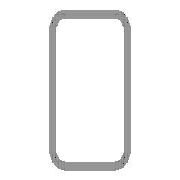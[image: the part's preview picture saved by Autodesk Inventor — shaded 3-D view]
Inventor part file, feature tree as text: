
AUTODESK INVENTOR PART (.ipt)
format: ipt  version: 2025.3 (Build 293356000, 356)  size: 149,504 bytes
history: native  units: mm (DEFAULTED — no unit token found)
features: other x4, plane x3, split x2, sketch x1
ambient origin geometry x8: Origin, YZ Plane, XZ Plane, XY Plane, X Axis, Y Axis, Z Axis, Center Point
bodies: Solid1 (feature_tree), Body (feature_tree)
feature tree (10):
  parser-record x1  (decoder bookkeeping rows leaked as tree rows — omitted from the tree; the rows remain in map.json)
  other  "Driven Length"
  other  "Start Plane"
  other  "End Plane"
  plane  "Work Plane4"
  split  "Split1"
  plane  "Work Plane5"
  split  "Split2"
  sketch  "Sketch3"  dims[d3=1042.584582mm d4=0.0mm d7=6.0mm d9=40.0mm d11=80.0mm d12=3.0mm d13=141.052102mm d14=1183.636683mm d15=20.0mm d16=40.0mm d17=90.0deg d18=1042.584582mm]
  plane  "Work Plane3"
